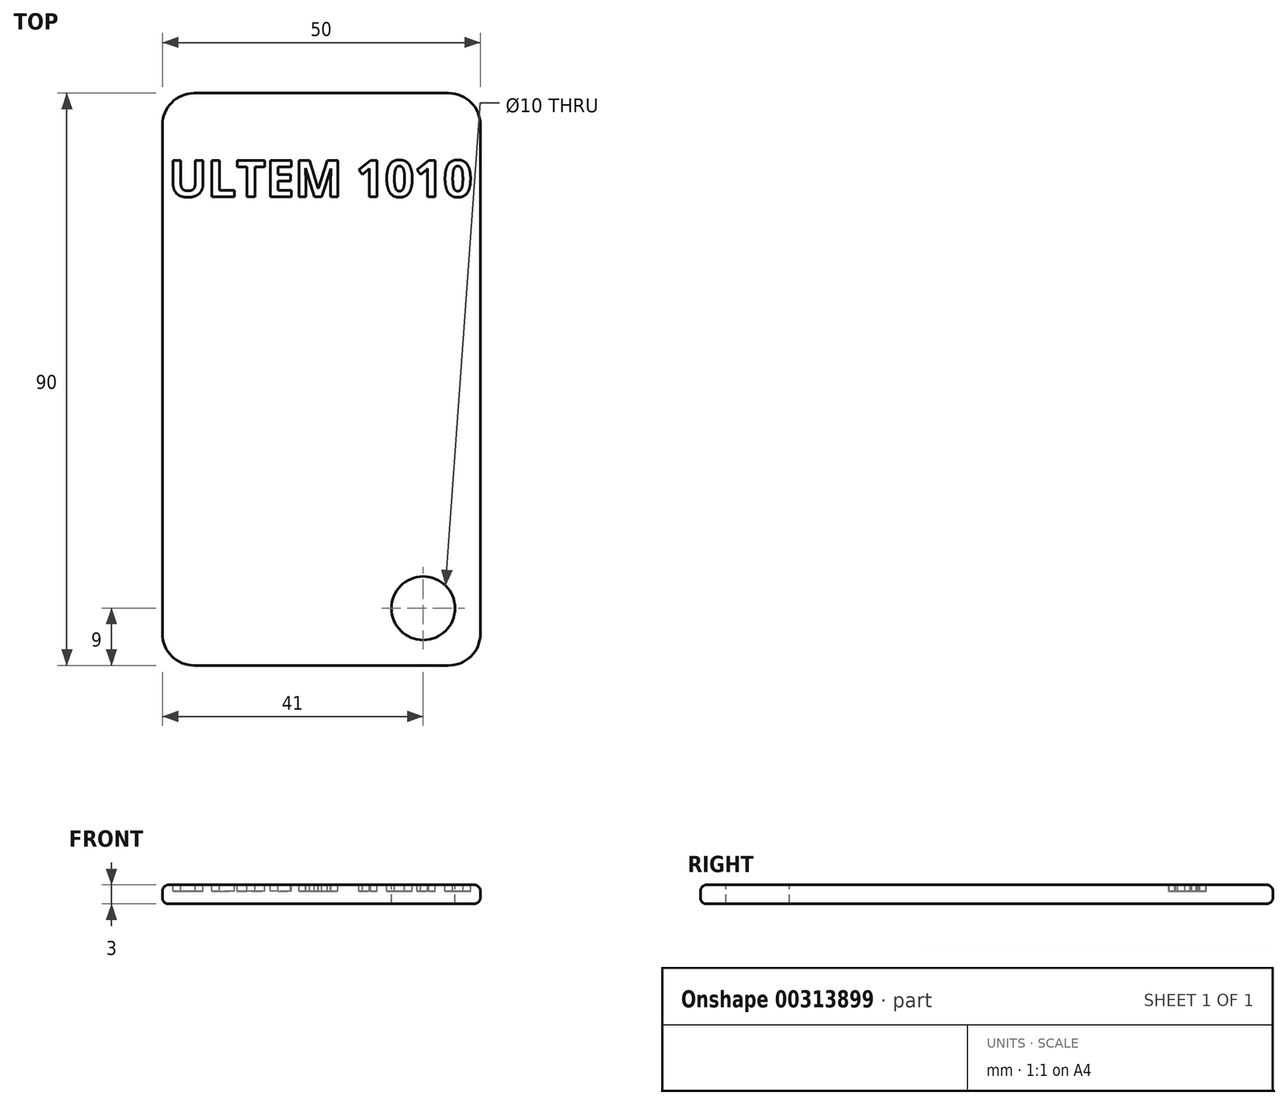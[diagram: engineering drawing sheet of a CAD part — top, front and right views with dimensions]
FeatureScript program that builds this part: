
annotation { "Feature Type Name" : "Feature", "Feature Type Description" : "" }
export const myFeature = defineFeature(function(context is Context, id is Id, definition is map)
    precondition{}
    {
        {
            var Q0;
            Q0=qCreatedBy(makeId("Top.planeOp"),FACE);
            var sketch = newSketch(context, id + "F0", { "sketchPlane" : qUnion([Q0])});
            skLineSegment(sketch, "E0.bottom", {"start": v(-45, 25) * mm, "end": v(45, 25) * mm});
            skLineSegment(sketch, "E0.top", {"start": v(-45, -25) * mm, "end": v(45, -25) * mm});
            skLineSegment(sketch, "E0.left", {"start": v(-45, 25) * mm, "end": v(-45, -25) * mm});
            skLineSegment(sketch, "E0.right", {"start": v(45, 25) * mm, "end": v(45, -25) * mm});
            skLineSegment(sketch, "E1", {"start": v(-45, 25) * mm, "end": v(45, -25) * mm, "construction": true});
            skSolve(sketch);
        }
        {
            var Q0;
            Q0=makeQuery(id+"F0.imprint","IMPRINT",FACE,{"disambiguationData":[TD([[makeQuery(id+"F0.imprint","IMPRINT",EDGE,{"derivedFrom":sQuery(id+"F0.wireOp",EDGE,"E0.bottom")}),-1.0]])]});
            extrude(context, id + "F1", {"entities" : qUnion([Q0]), "depth" : 3 * mm});
        }
        {
            var Q0;
            Q0=makeQuery(id+"F1.opExtrude","CAP_FACE",FACE,{"disambiguationData":[OSD([sQuery(id+"F0.wireOp",EDGE,"E0.bottom"),sQuery(id+"F0.wireOp",EDGE,"E0.top"),sQuery(id+"F0.wireOp",EDGE,"E0.left"),sQuery(id+"F0.wireOp",EDGE,"E0.right")])],"isStart":false});
            var Q1;
            Q1=makeQuery(id+"F1.opExtrude","CAP_FACE",FACE,{"disambiguationData":[OSD([sQuery(id+"F0.wireOp",EDGE,"E0.bottom"),sQuery(id+"F0.wireOp",EDGE,"E0.top"),sQuery(id+"F0.wireOp",EDGE,"E0.left"),sQuery(id+"F0.wireOp",EDGE,"E0.right")])],"isStart":true});
            fillet(context, id + "F2", {"entities" : qUnion([Q0, Q1]), "radius" : 1 * mm, "tangentPropagation" : true, "allowEdgeOverflow" : false});
        }
        {
            var Q0;
            Q0=makeQuery(id+"F1.opExtrude","SWEPT_EDGE",EDGE,{"disambiguationData":[OSD([sQuery(id+"F0.wireOp",EDGE,"E0.top"),sQuery(id+"F0.wireOp",EDGE,"E0.right")])]});
            var Q1;
            Q1=makeQuery(id+"F1.opExtrude","SWEPT_EDGE",EDGE,{"disambiguationData":[OSD([sQuery(id+"F0.wireOp",EDGE,"E0.bottom"),sQuery(id+"F0.wireOp",EDGE,"E0.right")])]});
            var Q2;
            Q2=makeQuery(id+"F1.opExtrude","SWEPT_EDGE",EDGE,{"disambiguationData":[OSD([sQuery(id+"F0.wireOp",EDGE,"E0.bottom"),sQuery(id+"F0.wireOp",EDGE,"E0.left")])]});
            var Q3;
            Q3=makeQuery(id+"F1.opExtrude","SWEPT_EDGE",EDGE,{"disambiguationData":[OSD([sQuery(id+"F0.wireOp",EDGE,"E0.top"),sQuery(id+"F0.wireOp",EDGE,"E0.left")])]});
            fillet(context, id + "F3", {"entities" : qUnion([Q0, Q1, Q2, Q3]), "radius" : 5 * mm, "tangentPropagation" : true, "allowEdgeOverflow" : false});
        }
        {
            var Q0;
            Q0=qCreatedBy(makeId("Right.planeOp"),FACE);
            var sketch = newSketch(context, id + "F4", { "sketchPlane" : qUnion([Q0])});
            skLineSegment(sketch, "E2", {"start": v(0, 0) * mm, "end": v(0, 32.9) * mm});
            skSolve(sketch);
        }
        {
            var Q0;
            Q0=makeQuery(id+"F1.opExtrude","SWEPT_BODY",BODY,{"disambiguationData":[OSD([sQuery(id+"F0.wireOp",EDGE,"E0.bottom"),sQuery(id+"F0.wireOp",EDGE,"E0.top"),sQuery(id+"F0.wireOp",EDGE,"E0.left"),sQuery(id+"F0.wireOp",EDGE,"E0.right")])]});
            var Q1;
            Q1=sQuery(id+"F4.wireOp",EDGE,"E2");
            transform(context, id + "F5", {"entities" : qUnion([Q0]), "transformType" : TransformType.ROTATION, "transformAxis" : qUnion([Q1]), "angle" : 90 * degree, "makeCopy" : false});
        }
        {
            var Q0;
            Q0=makeQuery(id+"F1.opExtrude","CAP_FACE",FACE,{"disambiguationData":[OSD([sQuery(id+"F0.wireOp",EDGE,"E0.bottom"),sQuery(id+"F0.wireOp",EDGE,"E0.top"),sQuery(id+"F0.wireOp",EDGE,"E0.left"),sQuery(id+"F0.wireOp",EDGE,"E0.right")])],"isStart":false});
            var sketch = newSketch(context, id + "F6", { "sketchPlane" : qUnion([Q0])});
            skText(sketch, "E3", { "text": "ULTEM 1010", "fontName": "OpenSans-Bold.ttf"});
            const initialGuessF6  = {"E3": [-0.024, 0.0287, 1, 0, 0.00578]};
            skSetInitialGuess(sketch, initialGuessF6);
            skSolve(sketch);
        }
        {
            var Q0;
            Q0=qSketchRegion(id+"F6",true);
            extrude(context, id + "F7", {"entities" : qUnion([Q0]), "operationType" : NewBodyOperationType.REMOVE, "oppositeDirection" : true, "depth" : 1 * mm});
        }
        {
            var Q0;
            {var subQ0=sQuery(id+"F0.wireOp",EDGE,"E0.left");var subQ2=sQuery(id+"F0.wireOp",EDGE,"E0.bottom");var subQ4=sQuery(id+"F0.wireOp",EDGE,"E0.right");var subQ6=sQuery(id+"F0.wireOp",EDGE,"E0.top");Q0=makeQuery(id+"F7.boolean.opBoolean","SPLIT",FACE,{"disambiguationData":[TD([makeQuery(id+"F7.opExtrude","SWEPT_FACE",FACE,{"disambiguationData":[OSD([sQuery(id+"F6.wireOp",EDGE,"E3.sketch_text.stroke-0")])]})])],"derivedFrom":makeQuery(id+"F1.opExtrude","CAP_FACE",FACE,{"disambiguationData":[OSD([subQ2,subQ6,subQ0,subQ4])],"isStart":false})});}
            var sketch = newSketch(context, id + "F8", { "sketchPlane" : qUnion([Q0])});
            skCircle(sketch, "E4", {"center": v(16, -36) * mm, "radius": 5 * mm});
            skSolve(sketch);
        }
        {
            var Q0;
            Q0=qSketchRegion(id+"F8",true);
            extrude(context, id + "F9", {"entities" : qUnion([Q0]), "operationType" : NewBodyOperationType.REMOVE, "oppositeDirection" : true, "depth" : 3 * mm});
        }
    });
